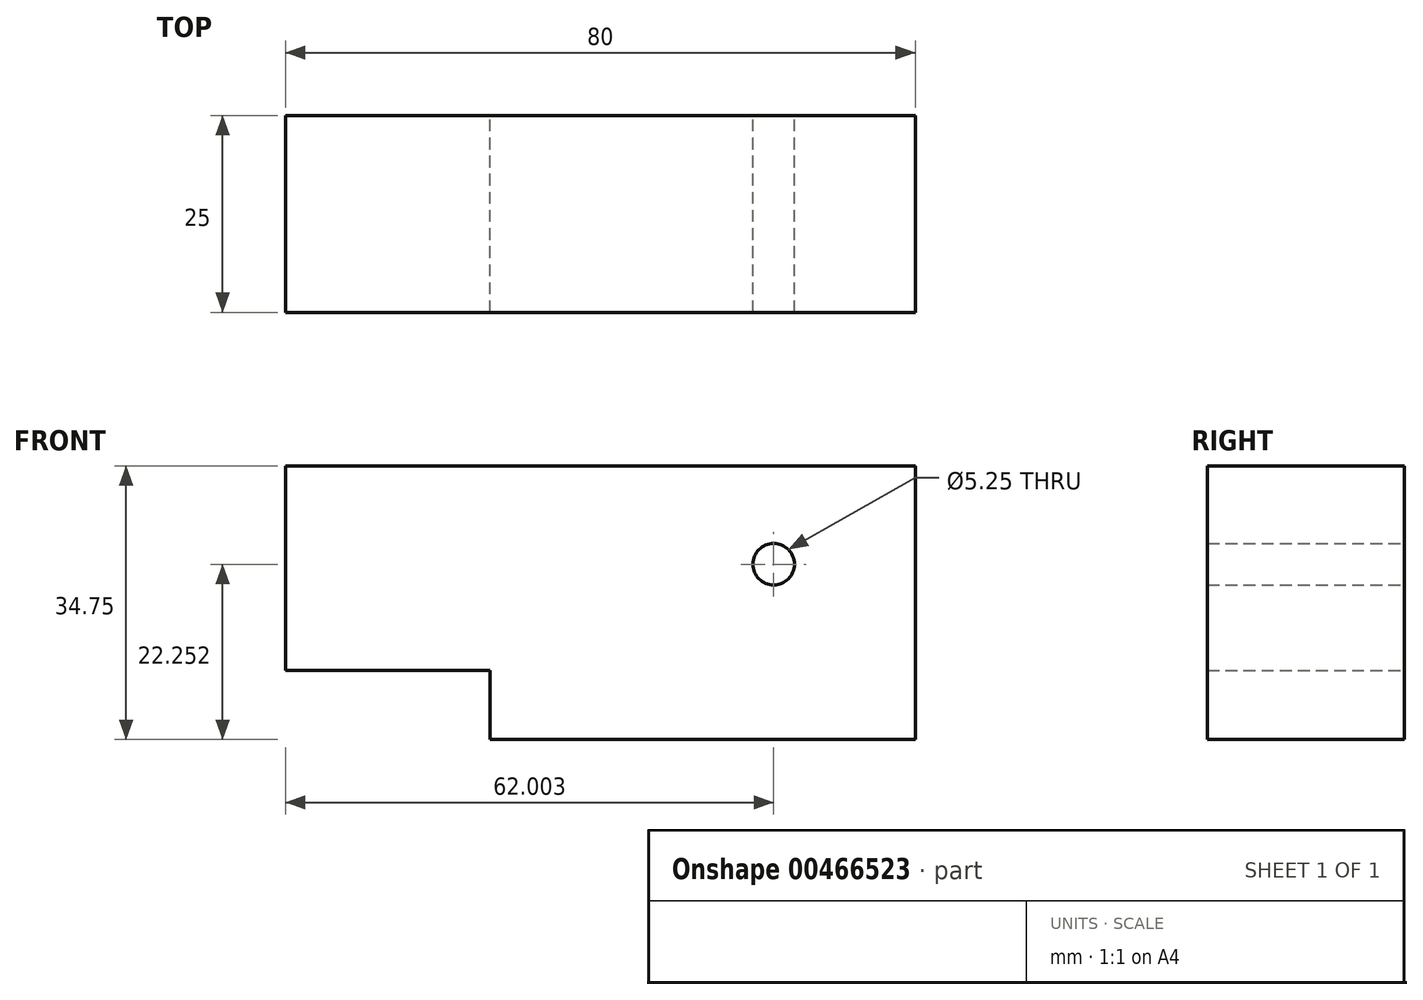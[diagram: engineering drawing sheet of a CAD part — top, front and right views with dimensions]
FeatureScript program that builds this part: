
annotation { "Feature Type Name" : "Feature", "Feature Type Description" : "" }
export const myFeature = defineFeature(function(context is Context, id is Id, definition is map)
    precondition{}
    {
        {
            var Q0;
            Q0=qCreatedBy(makeId("Front.planeOp"),FACE);
            var sketch = newSketch(context, id + "F0", { "sketchPlane" : qUnion([Q0]), "disableImprinting" : false});
            skLineSegment(sketch, "E0.bottom", {"start": v(25.9, -0.39) * mm, "end": v(79.9, -0.39) * mm});
            skLineSegment(sketch, "E0.top", {"start": v(-0.1, 34.36) * mm, "end": v(79.9, 34.36) * mm});
            skLineSegment(sketch, "E0.left", {"start": v(-0.1, 8.36) * mm, "end": v(-0.1, 34.36) * mm});
            skLineSegment(sketch, "E0.right", {"start": v(79.9, -0.39) * mm, "end": v(79.9, 34.36) * mm});
            skCircle(sketch, "E1", {"center": v(61.9, 21.86) * mm, "radius": 2.62 * mm});
            skLineSegment(sketch, "E2", {"start": v(-0.1, 8.36) * mm, "end": v(25.9, 8.36) * mm});
            skLineSegment(sketch, "E3", {"start": v(25.9, 8.36) * mm, "end": v(25.9, -0.39) * mm});
            skSolve(sketch);
        }
        {
            var Q0;
            Q0 = qSketchRegion(id + "F0", true);
            extrude(context, id + "F1", {"entities" : qUnion([Q0]), "depth" : 25 * mm});
        }
    });
